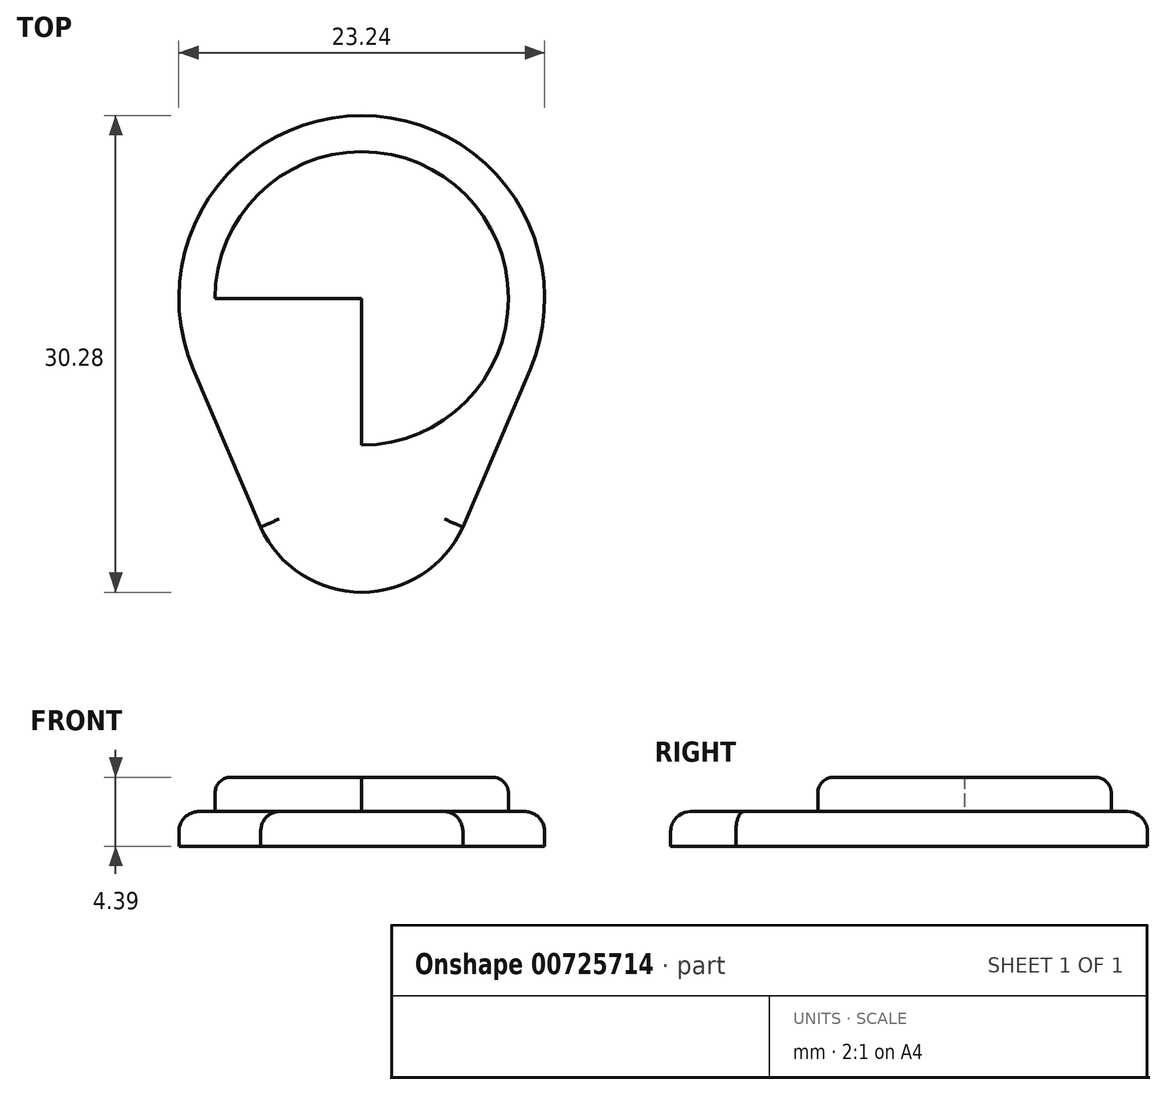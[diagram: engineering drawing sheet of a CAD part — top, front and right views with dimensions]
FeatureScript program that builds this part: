
annotation { "Feature Type Name" : "Feature", "Feature Type Description" : "" }
export const myFeature = defineFeature(function(context is Context, id is Id, definition is map)
    precondition{}
    {
        {
            var Q0;
            Q0=qCreatedBy(makeId("Top.planeOp"),FACE);
            var sketch = newSketch(context, id + "F0", { "sketchPlane" : qUnion([Q0])});
            skCircle(sketch, "E0", {"center": v(0, 26.76) * mm, "radius": 11.62 * mm});
            skCircle(sketch, "E1", {"center": v(0, 15.14) * mm, "radius": 7.05 * mm});
            skLineSegment(sketch, "E2", {"start": v(-10.68, 22.2) * mm, "end": v(-6.42, 12.23) * mm});
            skLineSegment(sketch, "E3", {"start": v(-6.42, 12.23) * mm, "end": v(6.42, 12.23) * mm});
            skLineSegment(sketch, "E4", {"start": v(6.42, 12.23) * mm, "end": v(10.68, 22.2) * mm});
            skSolve(sketch);
        }
        {
            var Q0;
            {var subQ0=sQuery(id+"F0.wireOp",EDGE,"E0");var subQ1=makeQuery(id+"F0.imprint","INTERSECT",VERTEX,{"derivedFrom":[subQ0,sQuery(id+"F0.wireOp",EDGE,"E2")]});Q0=makeQuery(id+"F0.imprint","IMPRINT",FACE,{"disambiguationData":[TD([[makeQuery(id+"F0.imprint","IMPRINT",EDGE,{"disambiguationData":[TD([[subQ1,-1.0]])],"derivedFrom":subQ0}),1.0]])]});}
            var Q1;
            {var subQ0=sQuery(id+"F0.wireOp",EDGE,"E1");var subQ1=sQuery(id+"F0.wireOp",EDGE,"E0");var subQ2=makeQuery(id+"F0.imprint","INTERSECT",VERTEX,{"disambiguationData":[OD(0.0)],"derivedFrom":[subQ1,subQ0]});Q1=makeQuery(id+"F0.imprint","IMPRINT",FACE,{"disambiguationData":[TD([[makeQuery(id+"F0.imprint","IMPRINT",EDGE,{"disambiguationData":[TD([[subQ2,-1.0]])],"derivedFrom":subQ1}),1.0]])]});}
            var Q2;
            {var subQ8=sQuery(id+"F0.wireOp",EDGE,"E3");Q2=makeQuery(id+"F0.imprint","IMPRINT",FACE,{"disambiguationData":[TD([[makeQuery(id+"F0.imprint","IMPRINT",EDGE,{"derivedFrom":subQ8}),1.0]])]});}
            var Q3;
            {var subQ0=sQuery(id+"F0.wireOp",EDGE,"E2");var subQ1=sQuery(id+"F0.wireOp",EDGE,"E0");var subQ2=makeQuery(id+"F0.imprint","INTERSECT",VERTEX,{"derivedFrom":[subQ1,subQ0]});Q3=makeQuery(id+"F0.imprint","IMPRINT",FACE,{"disambiguationData":[TD([[makeQuery(id+"F0.imprint","IMPRINT",EDGE,{"disambiguationData":[TD([[subQ2,-1.0]])],"derivedFrom":subQ1}),-1.0]])]});}
            var Q4;
            {var subQ0=sQuery(id+"F0.wireOp",EDGE,"E3");Q4=makeQuery(id+"F0.imprint","IMPRINT",FACE,{"disambiguationData":[TD([[makeQuery(id+"F0.imprint","IMPRINT",EDGE,{"derivedFrom":subQ0}),-1.0]])]});}
            var Q5;
            {var subQ0=sQuery(id+"F0.wireOp",EDGE,"E4");var subQ1=sQuery(id+"F0.wireOp",EDGE,"E0");var subQ2=makeQuery(id+"F0.imprint","INTERSECT",VERTEX,{"derivedFrom":[subQ1,subQ0]});Q5=makeQuery(id+"F0.imprint","IMPRINT",FACE,{"disambiguationData":[TD([[makeQuery(id+"F0.imprint","IMPRINT",EDGE,{"disambiguationData":[TD([[subQ2,1.0]])],"derivedFrom":subQ1}),-1.0]])]});}
            extrude(context, id + "F1", {"entities" : qUnion([Q0, Q1, Q2, Q3, Q4, Q5]), "depth" : 2.2 * mm, "offsetDistance" : 25.4 * mm});
        }
        {
            var Q0;
            Q0=makeQuery(id+"F1.opExtrude","CAP_FACE",FACE,{"disambiguationData":[OSD([sQuery(id+"F0.wireOp",EDGE,"E0"),sQuery(id+"F0.wireOp",EDGE,"E1"),sQuery(id+"F0.wireOp",EDGE,"E2"),sQuery(id+"F0.wireOp",EDGE,"E4")])],"isStart":false});
            fillet(context, id + "F2", {"entities" : qUnion([Q0]), "radius" : 1.27 * mm, "tangentPropagation" : true, "allowEdgeOverflow" : false});
        }
        {
            var Q0;
            Q0=makeQuery(id+"F1.opExtrude","CAP_FACE",FACE,{"disambiguationData":[OSD([sQuery(id+"F0.wireOp",EDGE,"E0"),sQuery(id+"F0.wireOp",EDGE,"E1"),sQuery(id+"F0.wireOp",EDGE,"E2"),sQuery(id+"F0.wireOp",EDGE,"E4")])],"isStart":false});
            var sketch = newSketch(context, id + "F3", { "sketchPlane" : qUnion([Q0])});
            skLineSegment(sketch, "E5", {"start": v(0, 37.1) * mm, "end": v(0, 9.36) * mm});
            skCircle(sketch, "E6", {"center": v(0, 26.76) * mm, "radius": 9.32 * mm});
            skLineSegment(sketch, "E7", {"start": v(0, 26.76) * mm, "end": v(-9.32, 26.76) * mm});
            skSolve(sketch);
        }
        {
            var Q0;
            {var subQ0=sQuery(id+"F3.wireOp",EDGE,"E7");Q0=makeQuery(id+"F3.imprint","IMPRINT",FACE,{"disambiguationData":[TD([[makeQuery(id+"F3.imprint","IMPRINT",EDGE,{"derivedFrom":subQ0}),-1.0]])]});}
            var Q1;
            {var subQ0=sQuery(id+"F3.wireOp",EDGE,"E5");var subQ1=makeQuery(id+"F3.imprint","INTERSECT",VERTEX,{"derivedFrom":[subQ0,sQuery(id+"F3.wireOp",EDGE,"E7")]});Q1=makeQuery(id+"F3.imprint","IMPRINT",FACE,{"disambiguationData":[TD([[makeQuery(id+"F3.imprint","IMPRINT",EDGE,{"disambiguationData":[TD([[subQ1,1.0]])],"derivedFrom":subQ0}),1.0]])]});}
            extrude(context, id + "F4", {"entities" : qUnion([Q0, Q1]), "operationType" : NewBodyOperationType.ADD, "depth" : 2.18 * mm, "offsetDistance" : 25.4 * mm});
        }
        {
            var Q0;
            Q0=makeQuery(id+"F4.opExtrude","CAP_EDGE",EDGE,{"disambiguationData":[OSD([sQuery(id+"F3.wireOp",EDGE,"E6")])],"isStart":false});
            fillet(context, id + "F5", {"entities" : qUnion([Q0]), "radius" : 1.02 * mm, "tangentPropagation" : true, "allowEdgeOverflow" : false});
        }
    });
